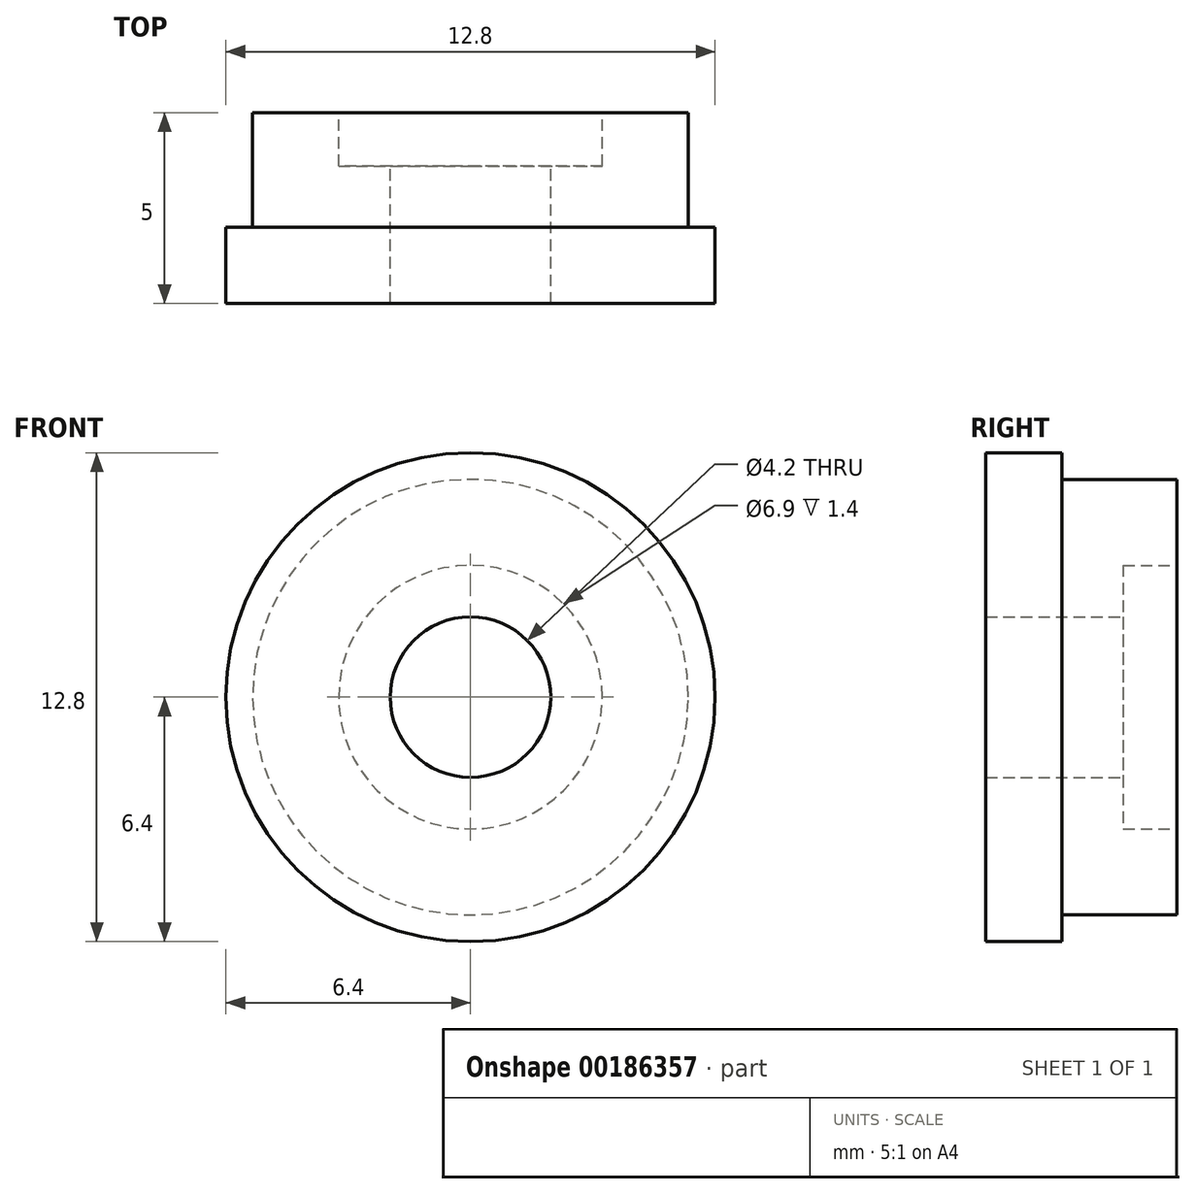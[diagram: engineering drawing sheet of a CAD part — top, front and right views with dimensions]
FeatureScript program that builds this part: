
annotation { "Feature Type Name" : "Feature", "Feature Type Description" : "" }
export const myFeature = defineFeature(function(context is Context, id is Id, definition is map)
    precondition{}
    {
        {
            var Q0;
            Q0=qCreatedBy(makeId("Right.planeOp"),FACE);
            var sketch = newSketch(context, id + "F0", { "sketchPlane" : qUnion([Q0])});
            skLineSegment(sketch, "E0", {"start": v(11.47, 0) * mm, "end": v(0, 0) * mm, "construction": true});
            skLineSegment(sketch, "E1", {"start": v(3.6, 2.1) * mm, "end": v(0, 2.1) * mm});
            skLineSegment(sketch, "E2", {"start": v(3.6, 2.1) * mm, "end": v(3.6, 3.45) * mm});
            skLineSegment(sketch, "E3", {"start": v(5, 3.45) * mm, "end": v(3.6, 3.45) * mm});
            skLineSegment(sketch, "E4", {"start": v(5, 3.45) * mm, "end": v(5, 5.7) * mm});
            skLineSegment(sketch, "E5", {"start": v(2, 5.7) * mm, "end": v(5, 5.7) * mm});
            skLineSegment(sketch, "E6", {"start": v(2, 5.7) * mm, "end": v(2, 6.4) * mm});
            skLineSegment(sketch, "E7", {"start": v(0, 6.4) * mm, "end": v(2, 6.4) * mm});
            skLineSegment(sketch, "E8", {"start": v(0, 6.4) * mm, "end": v(0, 2.1) * mm});
            skSolve(sketch);
        }
        {
            var Q0;
            Q0=makeQuery(id+"F0.imprint","IMPRINT",FACE,{"disambiguationData":[TD([[makeQuery(id+"F0.imprint","IMPRINT",EDGE,{"derivedFrom":sQuery(id+"F0.wireOp",EDGE,"E1")}),-1.0]])]});
            var Q1;
            Q1=sQuery(id+"F0.wireOp",EDGE,"E0");
            revolve(context, id + "F1", {"entities" : qUnion([Q0]), "axis" : qUnion([Q1]), "revolveType" : RevolveType.FULL});
        }
    });
